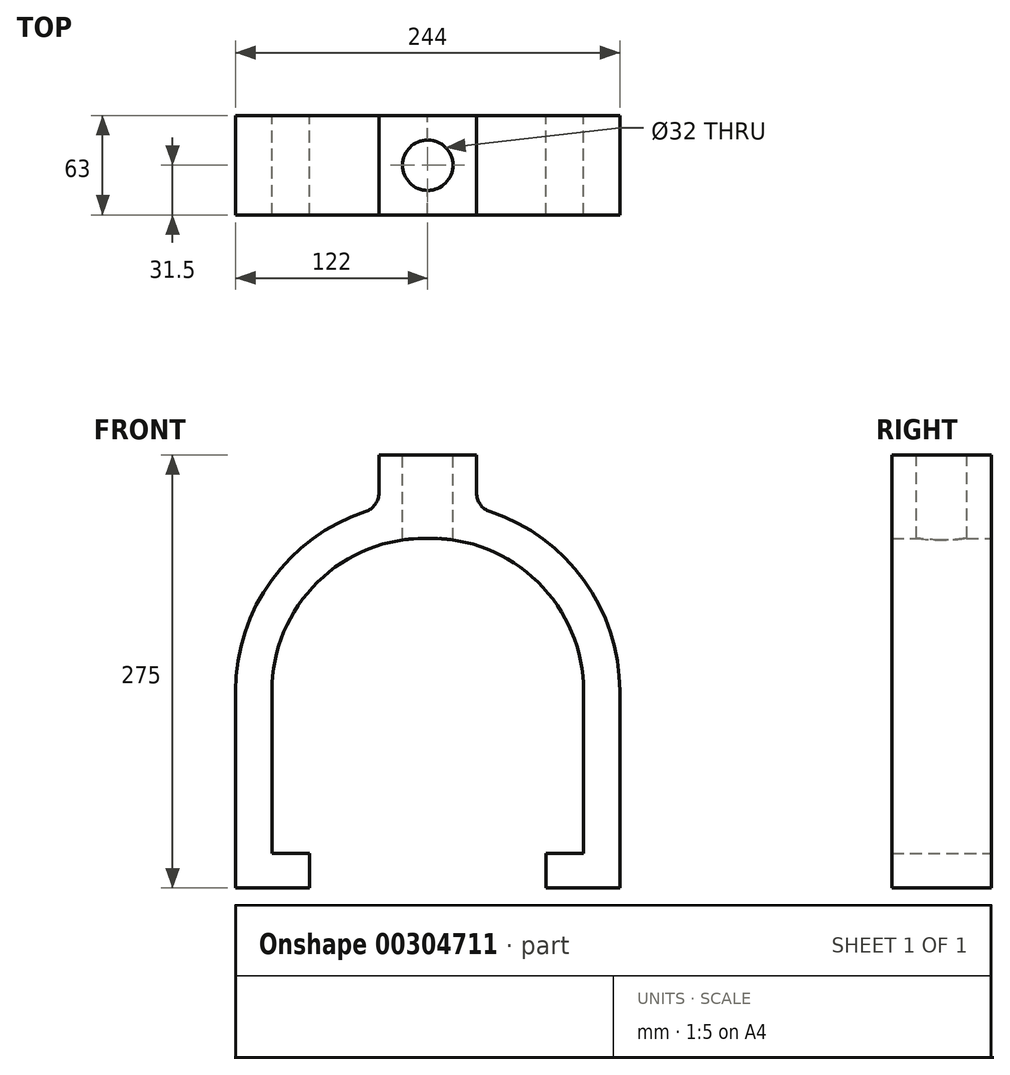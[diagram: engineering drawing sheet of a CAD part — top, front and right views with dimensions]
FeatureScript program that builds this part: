
annotation { "Feature Type Name" : "Feature", "Feature Type Description" : "" }
export const myFeature = defineFeature(function(context is Context, id is Id, definition is map)
    precondition{}
    {
        {
            var Q0;
            Q0=qCreatedBy(makeId("Front.planeOp"),FACE);
            var sketch = newSketch(context, id + "F0", { "sketchPlane" : qUnion([Q0])});
            skLineSegment(sketch, "E0", {"start": v(0, 0) * mm, "end": v(-122, 0) * mm, "construction": true});
            skLineSegment(sketch, "E1", {"start": v(-122, 0) * mm, "end": v(-122, 125) * mm});
            skLineSegment(sketch, "E2", {"start": v(-122, 0) * mm, "end": v(-75, 0) * mm});
            skLineSegment(sketch, "E3", {"start": v(-75, 0) * mm, "end": v(-75, 22) * mm});
            skLineSegment(sketch, "E4", {"start": v(-75, 22) * mm, "end": v(-99, 22) * mm});
            skLineSegment(sketch, "E5", {"start": v(-99, 22) * mm, "end": v(-99, 125) * mm});
            skLineSegment(sketch, "E6", {"start": v(0, 0) * mm, "end": v(0, 221.98) * mm, "construction": true});
            skArc(sketch, "E7", {"start": v(-99, 125) * mm, "mid": v(-69.88, 194.3) * mm, "end": v(0, 221.98) * mm});
            skArc(sketch, "E8", {"start": v(-122, 125) * mm, "mid": v(-99.24, 195.32) * mm, "end": v(-39.58, 238.96) * mm});
            skLineSegment(sketch, "E9", {"start": v(-31, 275) * mm, "end": v(-31, 250.83) * mm});
            skLineSegment(sketch, "E10", {"start": v(-31, 250.83) * mm, "end": v(-31, 275) * mm});
            skLineSegment(sketch, "E11", {"start": v(0, 275) * mm, "end": v(-31, 275) * mm});
            skPoint(sketch, "E12.newPointB", {"position": v(0, 244.98) * mm});
            skArc(sketch, "E12.filletArc", {"start": v(-39.58, 238.96) * mm, "mid": v(-33.37, 243.5) * mm, "end": v(-31, 250.83) * mm});
            skPoint(sketch, "E13.orphan", {"position": v(-31, 244.98) * mm});
            skLineSegment(sketch, "E14.MirrorCS", {"start": v(0, 275) * mm, "end": v(31, 275) * mm});
            skLineSegment(sketch, "E15.MirrorCS", {"start": v(31, 250.83) * mm, "end": v(31, 275) * mm});
            skArc(sketch, "E16.MirrorCS", {"start": v(39.58, 238.96) * mm, "mid": v(33.37, 243.5) * mm, "end": v(31, 250.83) * mm});
            skArc(sketch, "E17.MirrorCS", {"start": v(122, 125) * mm, "mid": v(99.24, 195.32) * mm, "end": v(39.58, 238.96) * mm});
            skArc(sketch, "E18.MirrorCS", {"start": v(99, 125) * mm, "mid": v(69.88, 194.3) * mm, "end": v(0, 221.98) * mm});
            skLineSegment(sketch, "E19.MirrorCS", {"start": v(122, 0) * mm, "end": v(122, 125) * mm});
            skLineSegment(sketch, "E20.MirrorCS", {"start": v(99, 22) * mm, "end": v(99, 125) * mm});
            skLineSegment(sketch, "E21.MirrorCS", {"start": v(75, 22) * mm, "end": v(99, 22) * mm});
            skLineSegment(sketch, "E22.MirrorCS", {"start": v(0, 0) * mm, "end": v(122, 0) * mm, "construction": true});
            skLineSegment(sketch, "E23.MirrorCS", {"start": v(75, 0) * mm, "end": v(75, 22) * mm});
            skLineSegment(sketch, "E24", {"start": v(122, 0) * mm, "end": v(75, 0) * mm});
            skSolve(sketch);
        }
        {
            var Q0;
            Q0 = qSketchRegion(id + "F0", true);
            extrude(context, id + "F1", {"entities" : qUnion([Q0]), "depth" : 63 * mm});
        }
        {
            var Q0;
            Q0=makeQuery(id+"F1.opExtrude","SWEPT_FACE",FACE,{"disambiguationData":[OSD([sQuery(id+"F0.wireOp",EDGE,"E11"),sQuery(id+"F0.wireOp",EDGE,"E14.MirrorCS")])]});
            var sketch = newSketch(context, id + "F2", { "sketchPlane" : qUnion([Q0])});
            skCircle(sketch, "E25", {"center": v(0, -31.5) * mm, "radius": 16 * mm});
            skSolve(sketch);
        }
        {
            var Q0;
            Q0 = qSketchRegion(id + "F2", true);
            extrude(context, id + "F3", {"entities" : qUnion([Q0]), "operationType" : NewBodyOperationType.REMOVE, "endBound" : BoundingType.THROUGH_ALL, "oppositeDirection" : true, "depth" : 25 * mm});
        }
    });
